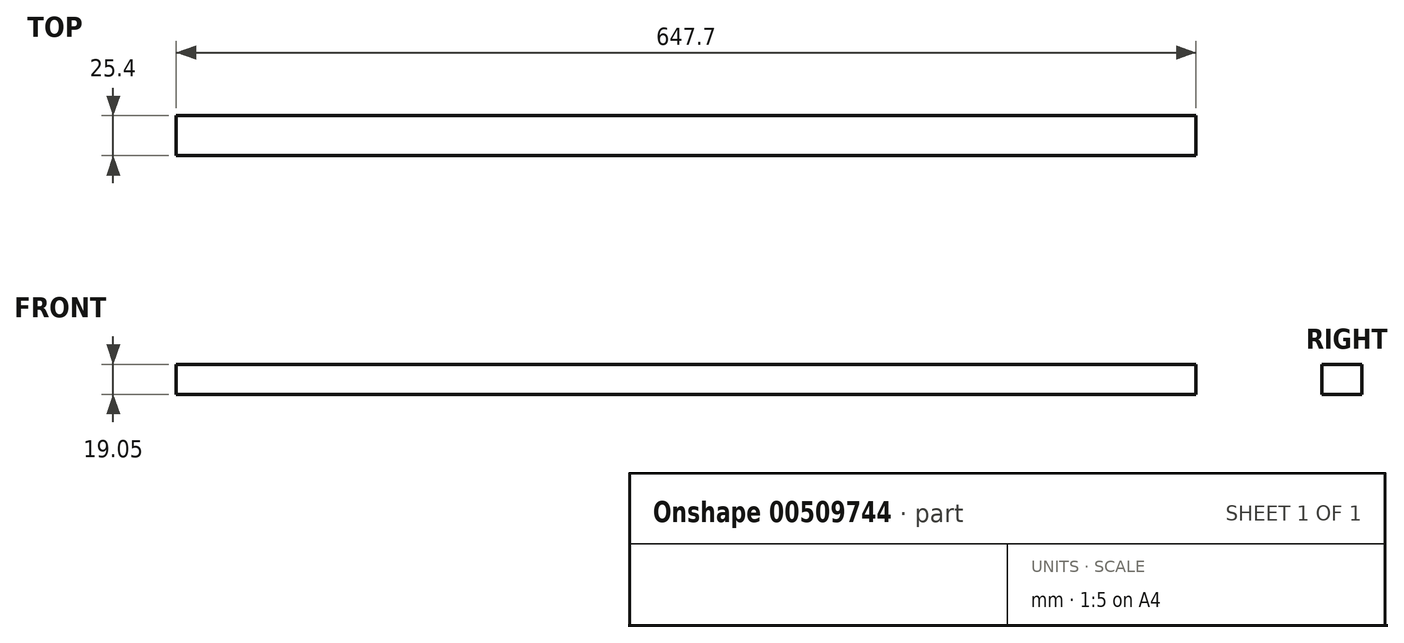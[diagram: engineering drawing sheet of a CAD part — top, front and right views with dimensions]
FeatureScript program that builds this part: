
annotation { "Feature Type Name" : "Feature", "Feature Type Description" : "" }
export const myFeature = defineFeature(function(context is Context, id is Id, definition is map)
    precondition{}
    {
        {
            var Q0;
            Q0=qCreatedBy(makeId("Front.planeOp"),FACE);
            var sketch = newSketch(context, id + "F0", { "sketchPlane" : qUnion([Q0])});
            skLineSegment(sketch, "E0.bottom", {"start": v(-283.3, 49.05) * mm, "end": v(364.4, 49.05) * mm});
            skLineSegment(sketch, "E0.top", {"start": v(-283.3, 30) * mm, "end": v(364.4, 30) * mm});
            skLineSegment(sketch, "E0.left", {"start": v(-283.3, 49.05) * mm, "end": v(-283.3, 30) * mm});
            skLineSegment(sketch, "E0.right", {"start": v(364.4, 49.05) * mm, "end": v(364.4, 30) * mm});
            skSolve(sketch);
        }
        {
            var Q0;
            Q0=qSketchRegion(id+"F0",true);
            extrude(context, id + "F1", {"entities" : qUnion([Q0]), "depth" : 25.4 * mm});
        }
    });
